# Revit family: LRTC 2x2_2x4
name_source: partatom
category: Lighting Fixtures
units: mm (PartAtom-declared; Revit-internal decimal feet)

## family parameters
Always vertical = Yes
Cut with Voids When Loaded = No
Host = Ceiling
Light Source = Yes
OmniClass Number = 23.80.70.11.14.17
OmniClass Title = Direct/Indirect
Part Type = Normal
Room Calculation Point = No
Round Connector Dimension = Use Diameter
Shared = No

## types (3) — shared parameters
Assembly Code = D5020200
Color Filter = 16777215
Description = LED Troffer Dish Single Tear Drop
Dimming Lamp Color Temperature Shift = <None>
Emit Shape Visible in Rendering = No
Emit from Rectangle Width = 1' - 11 3/4"
Housing Finish = Metal - Viscor - White
Lamp = LED
Lens Finish = Acrylic - Viscor - Frosted Ribbed Linear Extruded
Manufacturer = VISIONEERING by VISCOR
Model = LRTC
Reflector Width = 0' - 11 7/8"
Tilt Angle = 90.00°
URL = https://www.viscor.com
Voltage = 120 V
Width = 1' - 11 3/4"

## per-type parameters (varying)
| type | Apparent Load | Emit from Rectangle Length | Lamp Wattage | Length | Photometric Web File |
| LRTC2X2-LED840K020LUNV | 18 VA | 1' - 11 3/4" | 18 VA | 1' - 11 3/4" | LRTC2x2-LED840K020LUNV-G003581.IES |
| LRTC2x4-LED840K041LUNV | 39 VA | 3' - 11 3/4" | 39 VA | 3' - 11 3/4" | LRTC2X4-LED840K041LUNV-G001546.IES |
| LRTC2x4-LED840K034LUNV | 30 VA | 3' - 11 3/4" | 30 VA | 3' - 11 3/4" | LRTC2X4-LED840K034LUNV-G001538.IES |

## geometry (parser evidence)
native form markers: Sweep x4
no freeform markers — native parametric forms only
